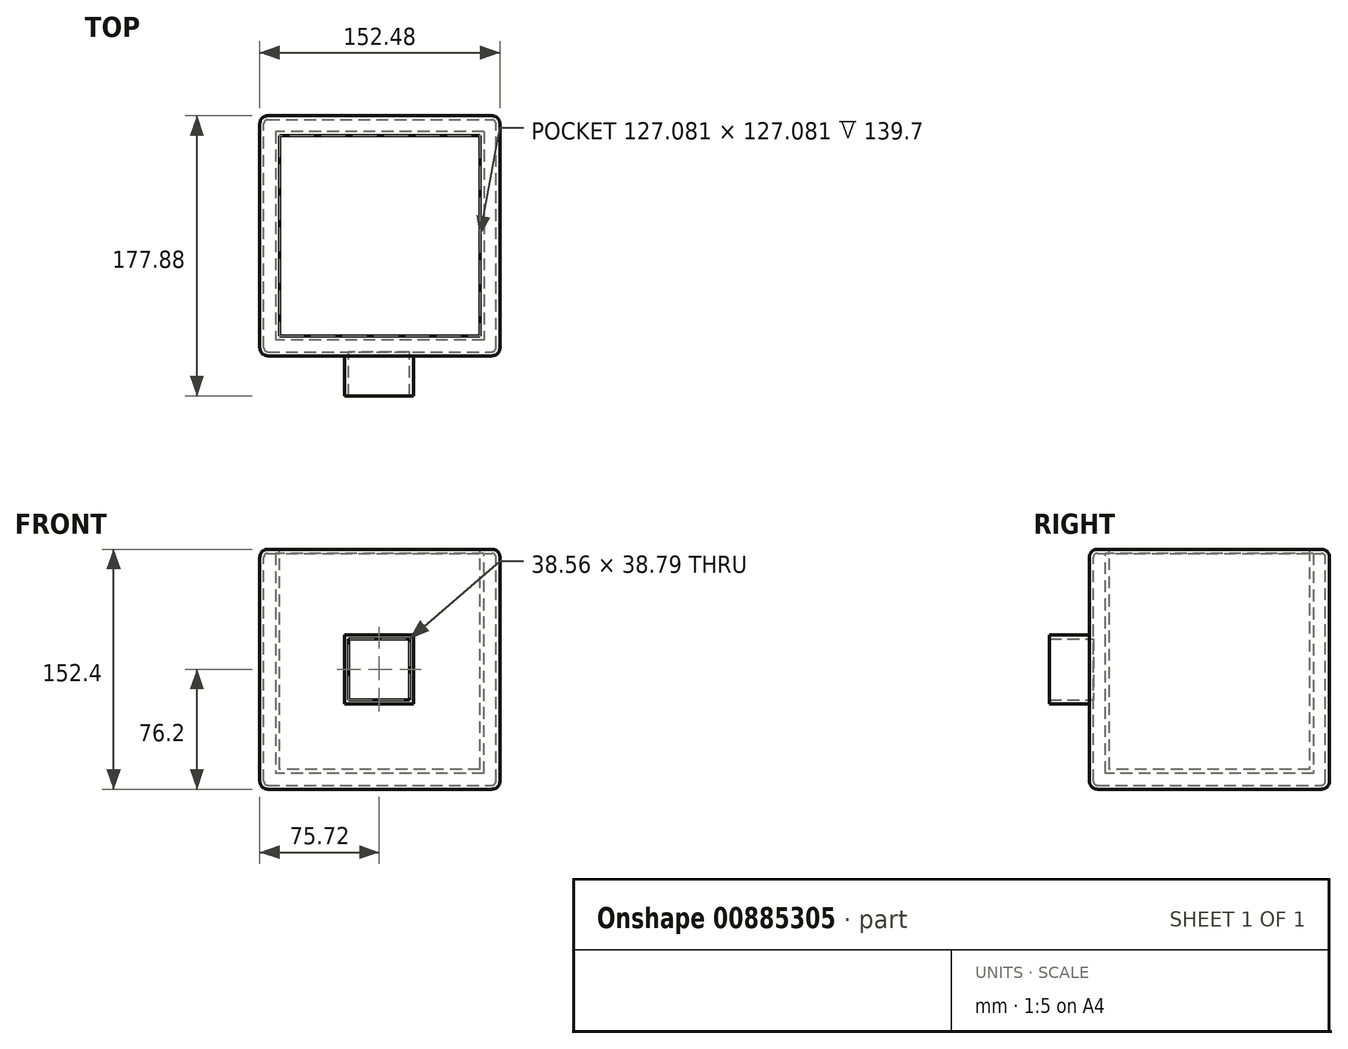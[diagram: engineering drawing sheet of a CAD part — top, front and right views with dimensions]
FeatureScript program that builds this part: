
annotation { "Feature Type Name" : "Feature", "Feature Type Description" : "" }
export const myFeature = defineFeature(function(context is Context, id is Id, definition is map)
    precondition{}
    {
        {
            var Q0;
            Q0=qCreatedBy(makeId("Top.planeOp"),FACE);
            var sketch = newSketch(context, id + "F0", { "sketchPlane" : qUnion([Q0])});
            skLineSegment(sketch, "E0.bottom", {"start": v(-75.72, -76.34) * mm, "end": v(76.76, -76.34) * mm});
            skLineSegment(sketch, "E0.top", {"start": v(-75.72, 76.14) * mm, "end": v(76.76, 76.14) * mm});
            skLineSegment(sketch, "E0.left", {"start": v(-75.72, -76.34) * mm, "end": v(-75.72, 76.14) * mm});
            skLineSegment(sketch, "E0.right", {"start": v(76.76, -76.34) * mm, "end": v(76.76, 76.14) * mm});
            skSolve(sketch);
        }
        {
            var Q0;
            Q0=makeQuery(id+"F0.imprint","IMPRINT",FACE,{"disambiguationData":[TD([[makeQuery(id+"F0.imprint","IMPRINT",EDGE,{"derivedFrom":sQuery(id+"F0.wireOp",EDGE,"E0.bottom")}),1.0]])]});
            extrude(context, id + "F1", {"entities" : qUnion([Q0]), "depth" : 76.2 * mm, "offsetDistance" : 25.4 * mm});
        }
        {
            var Q0;
            Q0=makeQuery(id+"F1.opExtrude","CAP_FACE",FACE,{"disambiguationData":[OSD([sQuery(id+"F0.wireOp",EDGE,"E0.bottom"),sQuery(id+"F0.wireOp",EDGE,"E0.top"),sQuery(id+"F0.wireOp",EDGE,"E0.left"),sQuery(id+"F0.wireOp",EDGE,"E0.right")])],"isStart":false});
            extrude(context, id + "F2", {"entities" : qUnion([Q0]), "operationType" : NewBodyOperationType.ADD, "oppositeDirection" : true, "depth" : 152.4 * mm, "offsetDistance" : 25.4 * mm});
        }
        {
            var Q0;
            Q0=makeQuery(id+"F2.opExtrude","CAP_EDGE",EDGE,{"disambiguationData":[OSD([sQuery(id+"F0.wireOp",EDGE,"E0.bottom")])],"isStart":false});
            var Q1;
            Q1=makeQuery(id+"F2.opExtrude","CAP_EDGE",EDGE,{"disambiguationData":[OSD([sQuery(id+"F0.wireOp",EDGE,"E0.right")])],"isStart":false});
            var Q2;
            {var subQ0=sQuery(id+"F0.wireOp",EDGE,"E0.bottom");Q2=makeQuery(id+"F2.boolean.opBoolean","MERGE",FACE,{"derivedFrom":[makeQuery(id+"F1.opExtrude","SWEPT_FACE",FACE,{"disambiguationData":[OSD([subQ0])]}),makeQuery(id+"F2.opExtrude","SWEPT_FACE",FACE,{"disambiguationData":[OSD([subQ0])]})]});}
            var Q3;
            Q3=makeQuery(id+"F1.opExtrude","CAP_FACE",FACE,{"disambiguationData":[OSD([sQuery(id+"F0.wireOp",EDGE,"E0.bottom"),sQuery(id+"F0.wireOp",EDGE,"E0.top"),sQuery(id+"F0.wireOp",EDGE,"E0.left"),sQuery(id+"F0.wireOp",EDGE,"E0.right")])],"isStart":false});
            var Q4;
            {var subQ0=sQuery(id+"F0.wireOp",EDGE,"E0.left");var subQ1=sQuery(id+"F0.wireOp",EDGE,"E0.bottom");Q4=makeQuery(id+"F2.boolean.opBoolean","MERGE",EDGE,{"derivedFrom":[makeQuery(id+"F1.opExtrude","SWEPT_EDGE",EDGE,{"disambiguationData":[OSD([subQ1,subQ0])]}),makeQuery(id+"F2.opExtrude","SWEPT_EDGE",EDGE,{"disambiguationData":[OSD([subQ1,subQ0])]})]});}
            var Q5;
            Q5=makeQuery(id+"F2.opExtrude","CAP_EDGE",EDGE,{"disambiguationData":[OSD([sQuery(id+"F0.wireOp",EDGE,"E0.top")])],"isStart":false});
            var Q6;
            Q6=makeQuery(id+"F2.opExtrude","CAP_FACE",FACE,{"disambiguationData":[OSD([sQuery(id+"F0.wireOp",EDGE,"E0.bottom"),sQuery(id+"F0.wireOp",EDGE,"E0.top"),sQuery(id+"F0.wireOp",EDGE,"E0.left"),sQuery(id+"F0.wireOp",EDGE,"E0.right")])],"isStart":false});
            var Q7;
            {var subQ0=sQuery(id+"F0.wireOp",EDGE,"E0.top");Q7=makeQuery(id+"F2.boolean.opBoolean","MERGE",FACE,{"derivedFrom":[makeQuery(id+"F1.opExtrude","SWEPT_FACE",FACE,{"disambiguationData":[OSD([subQ0])]}),makeQuery(id+"F2.opExtrude","SWEPT_FACE",FACE,{"disambiguationData":[OSD([subQ0])]})]});}
            var Q8;
            {var subQ0=sQuery(id+"F0.wireOp",EDGE,"E0.left");var subQ1=sQuery(id+"F0.wireOp",EDGE,"E0.top");Q8=makeQuery(id+"F2.boolean.opBoolean","MERGE",EDGE,{"derivedFrom":[makeQuery(id+"F1.opExtrude","SWEPT_EDGE",EDGE,{"disambiguationData":[OSD([subQ1,subQ0])]}),makeQuery(id+"F2.opExtrude","SWEPT_EDGE",EDGE,{"disambiguationData":[OSD([subQ1,subQ0])]})]});}
            var Q9;
            {var subQ0=sQuery(id+"F0.wireOp",EDGE,"E0.right");var subQ1=sQuery(id+"F0.wireOp",EDGE,"E0.bottom");Q9=makeQuery(id+"F2.boolean.opBoolean","MERGE",EDGE,{"derivedFrom":[makeQuery(id+"F1.opExtrude","SWEPT_EDGE",EDGE,{"disambiguationData":[OSD([subQ1,subQ0])]}),makeQuery(id+"F2.opExtrude","SWEPT_EDGE",EDGE,{"disambiguationData":[OSD([subQ1,subQ0])]})]});}
            var Q10;
            {var subQ0=sQuery(id+"F0.wireOp",EDGE,"E0.right");var subQ1=sQuery(id+"F0.wireOp",EDGE,"E0.top");Q10=makeQuery(id+"F2.boolean.opBoolean","MERGE",EDGE,{"derivedFrom":[makeQuery(id+"F1.opExtrude","SWEPT_EDGE",EDGE,{"disambiguationData":[OSD([subQ1,subQ0])]}),makeQuery(id+"F2.opExtrude","SWEPT_EDGE",EDGE,{"disambiguationData":[OSD([subQ1,subQ0])]})]});}
            var Q11;
            {var subQ0=sQuery(id+"F0.wireOp",EDGE,"E0.right");Q11=makeQuery(id+"F2.boolean.opBoolean","MERGE",FACE,{"derivedFrom":[makeQuery(id+"F1.opExtrude","SWEPT_FACE",FACE,{"disambiguationData":[OSD([subQ0])]}),makeQuery(id+"F2.opExtrude","SWEPT_FACE",FACE,{"disambiguationData":[OSD([subQ0])]})]});}
            var Q12;
            Q12=makeQuery(id+"F2.opExtrude","CAP_EDGE",EDGE,{"disambiguationData":[OSD([sQuery(id+"F0.wireOp",EDGE,"E0.left")])],"isStart":false});
            var Q13;
            Q13=makeQuery(id+"F1.opExtrude","CAP_EDGE",EDGE,{"disambiguationData":[OSD([sQuery(id+"F0.wireOp",EDGE,"E0.left")])],"isStart":false});
            var Q14;
            Q14=makeQuery(id+"F1.opExtrude","CAP_EDGE",EDGE,{"disambiguationData":[OSD([sQuery(id+"F0.wireOp",EDGE,"E0.bottom")])],"isStart":false});
            var Q15;
            Q15=makeQuery(id+"F1.opExtrude","CAP_EDGE",EDGE,{"disambiguationData":[OSD([sQuery(id+"F0.wireOp",EDGE,"E0.right")])],"isStart":false});
            var Q16;
            {var subQ0=sQuery(id+"F0.wireOp",EDGE,"E0.left");Q16=makeQuery(id+"F2.boolean.opBoolean","MERGE",FACE,{"derivedFrom":[makeQuery(id+"F1.opExtrude","SWEPT_FACE",FACE,{"disambiguationData":[OSD([subQ0])]}),makeQuery(id+"F2.opExtrude","SWEPT_FACE",FACE,{"disambiguationData":[OSD([subQ0])]})]});}
            var Q17;
            Q17=makeQuery(id+"F1.opExtrude","CAP_EDGE",EDGE,{"disambiguationData":[OSD([sQuery(id+"F0.wireOp",EDGE,"E0.top")])],"isStart":false});
            fillet(context, id + "F3", {"entities" : qUnion([Q0, Q1, Q2, Q3, Q4, Q5, Q6, Q7, Q8, Q9, Q10, Q11, Q12, Q13, Q14, Q15, Q16, Q17]), "radius" : 5.08 * mm, "tangentPropagation" : true, "allowEdgeOverflow" : false});
        }
        {
            var Q0;
            Q0=makeQuery(id+"F1.opExtrude","CAP_FACE",FACE,{"disambiguationData":[OSD([sQuery(id+"F0.wireOp",EDGE,"E0.bottom"),sQuery(id+"F0.wireOp",EDGE,"E0.top"),sQuery(id+"F0.wireOp",EDGE,"E0.left"),sQuery(id+"F0.wireOp",EDGE,"E0.right")])],"isStart":false});
            shell(context, id + "F4", {"entities" : qUnion([Q0]), "thickness" : 12.7 * mm});
        }
        {
            var Q0;
            {var subQ0=sQuery(id+"F0.wireOp",EDGE,"E0.bottom");Q0=makeQuery(id+"F2.boolean.opBoolean","MERGE",FACE,{"derivedFrom":[makeQuery(id+"F1.opExtrude","SWEPT_FACE",FACE,{"disambiguationData":[OSD([subQ0])]}),makeQuery(id+"F2.opExtrude","SWEPT_FACE",FACE,{"disambiguationData":[OSD([subQ0])]})]});}
            var sketch = newSketch(context, id + "F5", { "sketchPlane" : qUnion([Q0])});
            skLineSegment(sketch, "E1.bottom", {"start": v(21.82, 21.93) * mm, "end": v(-21.82, 21.93) * mm});
            skLineSegment(sketch, "E1.top", {"start": v(21.82, -21.93) * mm, "end": v(-21.82, -21.93) * mm});
            skLineSegment(sketch, "E1.left", {"start": v(21.82, 21.93) * mm, "end": v(21.82, -21.93) * mm});
            skLineSegment(sketch, "E1.right", {"start": v(-21.82, 21.93) * mm, "end": v(-21.82, -21.93) * mm});
            skPoint(sketch, "E1.middle", {"position": v(0, 0) * mm});
            skSolve(sketch);
        }
        {
            var Q0;
            Q0=makeQuery(id+"F5.imprint","IMPRINT",FACE,{"disambiguationData":[TD([[makeQuery(id+"F5.imprint","IMPRINT",EDGE,{"derivedFrom":sQuery(id+"F5.wireOp",EDGE,"E1.bottom")}),1.0]])]});
            extrude(context, id + "F6", {"entities" : qUnion([Q0]), "operationType" : NewBodyOperationType.ADD, "depth" : 25.4 * mm, "offsetDistance" : 25.4 * mm});
        }
        {
            var Q0;
            Q0=makeQuery(id+"F6.opExtrude","CAP_FACE",FACE,{"disambiguationData":[OSD([sQuery(id+"F5.wireOp",EDGE,"E1.bottom"),sQuery(id+"F5.wireOp",EDGE,"E1.top"),sQuery(id+"F5.wireOp",EDGE,"E1.left"),sQuery(id+"F5.wireOp",EDGE,"E1.right")])],"isStart":false});
            shell(context, id + "F7", {"entities" : qUnion([Q0]), "thickness" : 2.54 * mm});
        }
    });
